# Revit family: IS_Ceraline_BD137_BIM_NL
name_source: partatom
category: Plumbing Fixtures
units: mm (PartAtom-declared; Revit-internal decimal feet)

## family parameters
Always vertical = No
Cut with Voids When Loaded = No
OmniClass Number = 23.45.55.17
OmniClass Title = Mixing Faucets
Part Type = Normal
Room Calculation Point = No
Round Connector Dimension = Use Diameter
Shared = No
Work Plane-Based = No

## types (1)
- BD137XG - CERALINE BASIN MIXER RIM-MOUNTED VESSEL CLICK WASTE 5L PER MINUTE - SILK BLACK
    Accesoires = https://www.idealstandard.nl
    Accessories = https://www.idealstandard.nl
    Afmetingen = 50 x 185 x 320 mm
    AfstandsEenheid = Millimeter
    Afwerking = seide schwarz
    AreaMeasurement = Internal
    AreaUnits = Millimeter
    Artikelnummer = BD137XG
    Artikelomschrijving = CERALINE WASCHTISCHMISCHER RIM-MONTIERTER BEHÄLTER CLICK ABFALL 5L PRO MINUTE - SEIDE SCHWARZ
    Artikelreferentie = CERALINE WASCHTISCHMISCHER RIM-MONTIERTER BEHÄLTER CLICK ABFALL 5L PRO MINUTE
    Auteur = Ideal Standard
    BIMObjectName = IS_IdealStandard_Washbasintaps_Ceraline_BD137
    BIMobject category = Sanitary
    BIMobject category code = Sanitary Taps & Mixer
    BIMobject main category = Sanitary
    BIMobject main category code = Sanitary
    BarCode = 3800861101505
    Barcode = 3800861101505
    Bedieningkraan = Handbuch
    Bedieningkraanwerk = einzelne Ebene
    Beschrijvinggarantie = Herstellergarantie
    BimObjectNaam = IS_IdealStandard_Washbasintaps_Ceraline_BD137
    Brand = Ideal Standard
    Brand url = http://www.idealstandard.nl
    Breedte = 50
    BrutoGewicht = 0
    Color = seide schwarz
    ConnectionType = plumbing
    Cost = 0 $
    CurrencyUnit = €
    CurrentRevision = 1
    Date of publishing = 01/07/2021
    Description = CERALINE BASIN MIXER RIM-MOUNTED VESSEL CLICK WASTE 5L PER MINUTE - SILK BLACK
    Diepte = 185 mm
    DikteMateriaal = Messing
    Douchebak = No
    DrainSize = 0 mm  [stored 0 ft]
    DurationUnit = Years
    DuurEenheid = Jaren
    Edition number = 1
    Eigenschappen = WASCHTISCHMISCHER RIM-MONTIERTER BEHÄLTER CLICK ABFALL 5L PRO MINUTE - SEIDE SCHWARZ
    FaucetFunction = Washbasin Mixer
    FaucetOperation = Manual Lever mixer
    FaucetTopDescription = Lever mixer
    FaucetType = Washbasin Mixer
    Features = BASIN MIXER RIM-MOUNTED VESSEL CLICK WASTE 5L PER MINUTE - SILK BLACK
    Finish = seide schwarz
    Functiekraanwerk = Einhebelgriff
    GTIN code = https://3800861101505
    Garantieunits = Jaren
    GemaaktOp = 22/07/2021
    Help = https://www.idealstandard.nl
    Hoogte = 320.5
    Hulp = https://www.idealstandard.nl
    IFC Classification = Sanitary Terminal
    IfcExportAs = IfcValveType
    IfcExportType = FAUCET
    InletConnectionSize = 0 mm  [stored 0 ft]
    Installatieinstructies = https://www.idealstandard.nl
    Installation instructions = https://www.idealstandard.nl
    InstallationInstructions = https://www.idealstandard.nl
    IsBuiltIn = No
    IsHighPressure = No
    Kleur = seide schwarz
    Lengte = 185 mm
    LinearUnits = Millimeters
    MainColor = SILK BLACK
    MaintenanceInformation = https://www.idealstandard.nl
    Manufacturer = Ideal Standard
    Manufacturer name = Ideal Standard
    ManufacturerURL = https://www.idealstandard.nl
    Masterformat 2014 Code = 41 14 33
    Masterformat 2014 Description = Mixer
    Materiaal = Messing
    Material = Brass
    Material main = Brass
    MaterialThickness = 0 mm  [stored 0 ft]
    Merk = Ideal Standard
    Model = BD137XG
    ModelNumber = BD137XG
    ModelReference = CERALINE BASIN MIXER RIM-MOUNTED VESSEL CLICK WASTE 5L PER MINUTE
    Montageinstuctie = https://www.idealstandard.nl
    NBS Reference Code = 45-35-70/335
    NBS Reference Description = Shower mixers
    Name = Washbasintaps_Ceraline_BD137_IdealStandard
    NettWeight = 1.91
    Nettogewicht = 1.91
    NominalHeight = 321 mm
    NominalLength = 185 mm
    NominalWidth = 50 mm
    Normen = Washbasintaps_Ceraline_BD137_IdealStandard
    OmniClass Code = 23-31 11 00
    OmniClass Description = Faucets
    OppervlakteEenheid = Millimeter
    OutletConnectionSize = 0 mm  [stored 0 ft]
    Overloop = 0 mm  [stored 0 ft]
    Product Guid = 9288610d-61d7-4b78-961e-eb3729dd9e2f
    Product SKU = BD137
    Product certification = https://www.idealstandard.nl
    Product data url = https://bimobject.com
    Product family = Ceraline
    Product group = Taps & Mixers
    Product name = CERALINE BASIN MIXER RIM-MOUNTED VESSEL CLICK WASTE 5L PER MINUTE
    Product url = https://www.idealstandard.nl
    ProductInformation = https://www.idealstandard.nl
    ProductSoort = Armaturen Mixer
    Productinformatie = https://www.idealstandard.nl
    QR code = http://bimobject.com
    Referentie = CERALINE BASIN MIXER RIM-MOUNTED VESSEL CLICK WASTE 5L PER MINUTE
    Revisie = 1
    Shape = Cylindrical
    Size = 50 x 185 x 320 mm
    Space = Internal
    SpareParts = https://www.idealstandard.nl
    Technical description = https://www.idealstandard.nl
    Telefoonnummer = 077 355 08 08
    TestPressure = 10 Bar
    Testdruk = 10 Bar
    Typeconnectie = Installation
    UNSPSC Code = 301815
    URL = https://www.idealstandard.nl
    Uniclass 1.4 Code = L725111
    Uniclass 1.4 Description = Mixers taps
    Uniclass 2.0 Code = PR-35-06-82
    Uniclass 2.0 Description = Shower Mixers
    Uniclass 2015 Code = Pr_40_20_87_98
    Uniclass 2015 Name = Washbasin taps
    Uniclass2015Code = Pr_40_20_87_98
    Uniclass2015Title = Washbasin taps
    Uniclass2015Version = v1.20
    Urlproducent = https://www.idealstandard.nl
    ValutaEenheid = Euro
    Versie = 1
    Version = 1
    Vervangingskosten = 0
    VolumeUnits = Liters
    Volumeunits = Liter
    Vorm = zylindrisch
    WRASURL = https://www.wrasapprovals.co.uk
    WarrantyDescription = manufacturer warranty
    WarrantyDurationParts = 5
    WarrantyDurationUnit = Years
    Wisselstukken = https://www.idealstandard.nl
    Youtube clip = https://www.youtube.com

note: [stored X ft] marks values corroborated as IEEE doubles in the binary element streams (Revit-internal decimal feet)

## geometry (parser evidence)
native form markers: Sweep x3
no freeform markers — native parametric forms only
